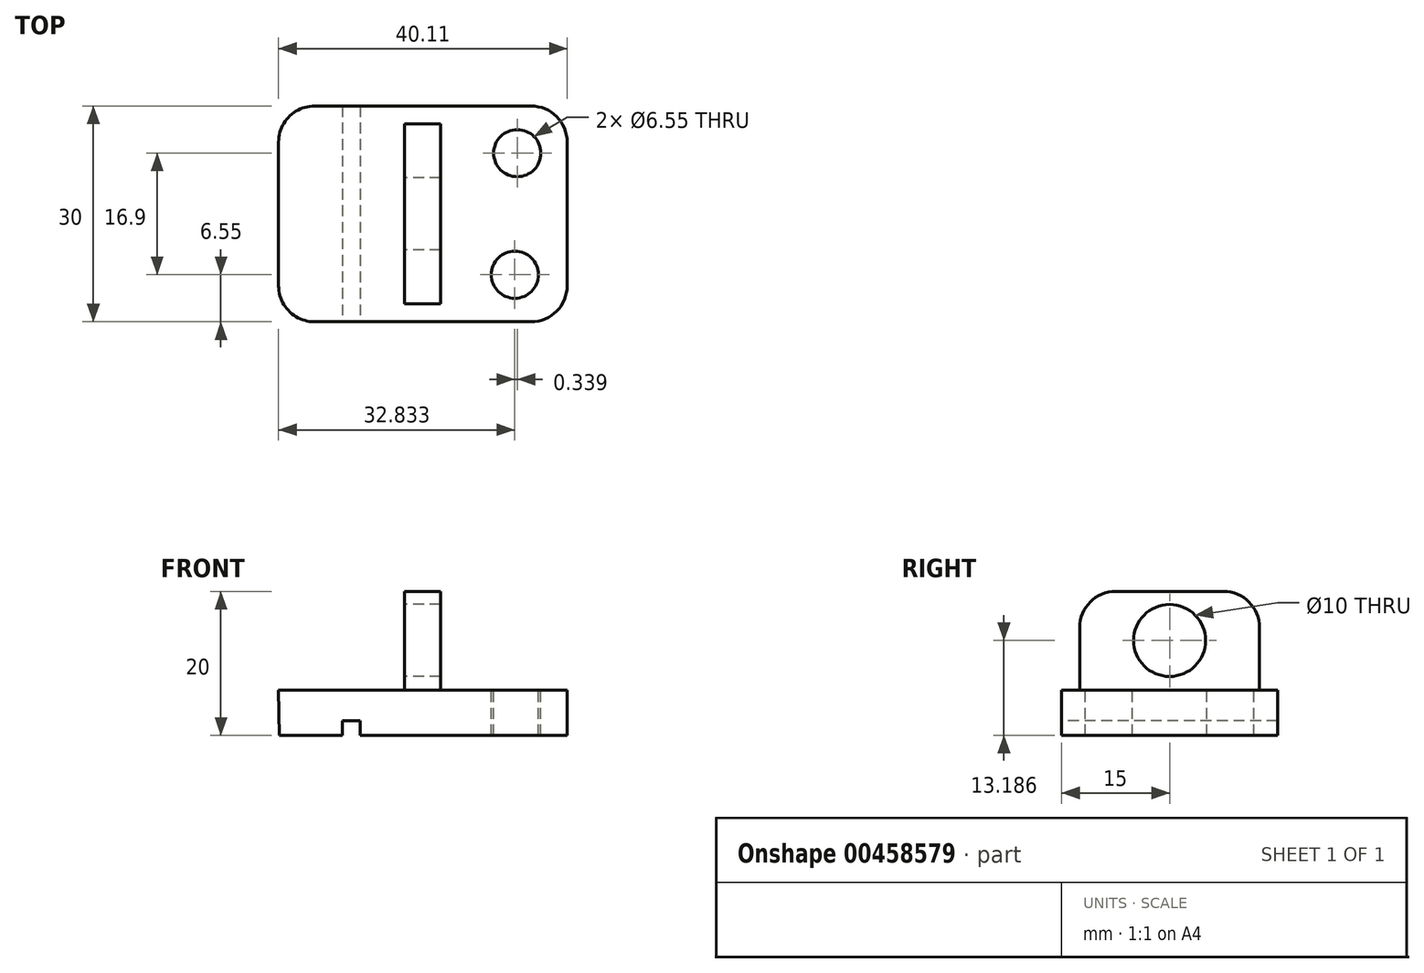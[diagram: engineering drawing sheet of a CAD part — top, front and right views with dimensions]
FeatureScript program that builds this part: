
annotation { "Feature Type Name" : "Feature", "Feature Type Description" : "" }
export const myFeature = defineFeature(function(context is Context, id is Id, definition is map)
    precondition{}
    {
        {
            var Q0;
            Q0=qCreatedBy(makeId("Front.planeOp"),FACE);
            var sketch = newSketch(context, id + "F0", { "sketchPlane" : qUnion([Q0])});
            skLineSegment(sketch, "E0", {"start": v(-11.08, -16.5) * mm, "end": v(29.03, -16.5) * mm});
            skLineSegment(sketch, "E1", {"start": v(29.03, -16.5) * mm, "end": v(29.03, -22.75) * mm});
            skLineSegment(sketch, "E2", {"start": v(29.03, -22.75) * mm, "end": v(-10.97, -22.75) * mm});
            skLineSegment(sketch, "E3", {"start": v(-10.97, -22.75) * mm, "end": v(-11.08, -16.5) * mm});
            skLineSegment(sketch, "E4", {"start": v(6.42, -16.5) * mm, "end": v(6.42, -2.75) * mm});
            skLineSegment(sketch, "E5", {"start": v(6.42, -2.75) * mm, "end": v(11.42, -2.75) * mm});
            skLineSegment(sketch, "E6", {"start": v(11.42, -2.75) * mm, "end": v(11.42, -16.5) * mm});
            skSolve(sketch);
        }
        {
            var Q0;
            {var subQ0=sQuery(id+"F0.wireOp",EDGE,"E1");Q0=makeQuery(id+"F0.imprint","IMPRINT",FACE,{"disambiguationData":[TD([[makeQuery(id+"F0.imprint","IMPRINT",EDGE,{"derivedFrom":subQ0}),-1.0]])]});}
            extrude(context, id + "F1", {"entities" : qUnion([Q0]), "endBound" : BoundingType.SYMMETRIC, "depth" : 30 * mm});
        }
        {
            var Q0;
            Q0 = qSketchRegion(id + "F0", true);
            extrude(context, id + "F2", {"entities" : qUnion([Q0]), "operationType" : NewBodyOperationType.ADD, "endBound" : BoundingType.SYMMETRIC, "depth" : 25 * mm});
        }
        {
            var Q0;
            Q0=qCreatedBy(makeId("Front.planeOp"),FACE);
            var sketch = newSketch(context, id + "F3", { "sketchPlane" : qUnion([Q0])});
            skLineSegment(sketch, "E7", {"start": v(-2.22, -22.75) * mm, "end": v(-2.22, -20.75) * mm});
            skLineSegment(sketch, "E8", {"start": v(-2.22, -20.75) * mm, "end": v(0.28, -20.75) * mm});
            skLineSegment(sketch, "E9", {"start": v(0.28, -20.75) * mm, "end": v(0.28, -22.75) * mm});
            skLineSegment(sketch, "E10", {"start": v(-2.22, -22.75) * mm, "end": v(0.28, -22.75) * mm});
            skSolve(sketch);
        }
        {
            var Q0;
            Q0=makeQuery(id+"F1.opExtrude","CAP_EDGE",EDGE,{"disambiguationData":[OSD([sQuery(id+"F0.wireOp",EDGE,"E1")])],"isStart":false});
            fillet(context, id + "F4", {"entities" : qUnion([Q0]), "radius" : 5 * mm, "tangentPropagation" : true, "allowEdgeOverflow" : false});
        }
        {
            var Q0;
            Q0=makeQuery(id+"F1.opExtrude","CAP_EDGE",EDGE,{"disambiguationData":[OSD([sQuery(id+"F0.wireOp",EDGE,"E1")])],"isStart":true});
            var Q1;
            Q1=makeQuery(id+"F1.opExtrude","CAP_EDGE",EDGE,{"disambiguationData":[OSD([sQuery(id+"F0.wireOp",EDGE,"E3")])],"isStart":false});
            var Q2;
            Q2=makeQuery(id+"F1.opExtrude","CAP_EDGE",EDGE,{"disambiguationData":[OSD([sQuery(id+"F0.wireOp",EDGE,"E3")])],"isStart":true});
            fillet(context, id + "F5", {"entities" : qUnion([Q0, Q1, Q2]), "radius" : 5 * mm, "tangentPropagation" : true, "allowEdgeOverflow" : false});
        }
        {
            var Q0;
            Q0=makeQuery(id+"F2.opExtrude","CAP_EDGE",EDGE,{"disambiguationData":[OSD([sQuery(id+"F0.wireOp",EDGE,"E5")])],"isStart":true});
            var Q1;
            Q1=makeQuery(id+"F2.opExtrude","CAP_EDGE",EDGE,{"disambiguationData":[OSD([sQuery(id+"F0.wireOp",EDGE,"E5")])],"isStart":false});
            fillet(context, id + "F6", {"entities" : qUnion([Q0, Q1]), "radius" : 5 * mm, "tangentPropagation" : true, "allowEdgeOverflow" : false});
        }
        {
            var Q0;
            Q0=qCreatedBy(makeId("Top.planeOp"),FACE);
            var sketch = newSketch(context, id + "F7", { "sketchPlane" : qUnion([Q0])});
            skCircle(sketch, "E11", {"center": v(21.75, -8.45) * mm, "radius": 3.28 * mm});
            skCircle(sketch, "E12", {"center": v(22.1, 8.45) * mm, "radius": 3.28 * mm});
            skSolve(sketch);
        }
        {
            var Q0;
            Q0=makeQuery(id+"F7.imprint","IMPRINT",FACE,{"disambiguationData":[TD([[makeQuery(id+"F7.imprint","IMPRINT",EDGE,{"derivedFrom":sQuery(id+"F7.wireOp",EDGE,"E12")}),1.0]])]});
            var Q1;
            Q1=makeQuery(id+"F7.imprint","IMPRINT",FACE,{"disambiguationData":[TD([[makeQuery(id+"F7.imprint","IMPRINT",EDGE,{"derivedFrom":sQuery(id+"F7.wireOp",EDGE,"E11")}),1.0]])]});
            extrude(context, id + "F8", {"entities" : qUnion([Q0, Q1]), "operationType" : NewBodyOperationType.REMOVE, "oppositeDirection" : true, "depth" : 25 * mm});
        }
        {
            var Q0;
            Q0 = qSketchRegion(id + "F3", true);
            extrude(context, id + "F9", {"entities" : qUnion([Q0]), "operationType" : NewBodyOperationType.REMOVE, "endBound" : BoundingType.SYMMETRIC, "oppositeDirection" : true, "depth" : 100 * mm});
        }
        {
            var Q0;
            Q0=qCreatedBy(makeId("Right.planeOp"),FACE);
            var sketch = newSketch(context, id + "F10", { "sketchPlane" : qUnion([Q0])});
            skCircle(sketch, "E13", {"center": v(0, -9.56) * mm, "radius": 5 * mm});
            skSolve(sketch);
        }
        {
            var Q0;
            Q0 = qSketchRegion(id + "F10", true);
            var Q1;
            Q1=sQuery(id+"F10.wireOp",EDGE,"E13");
            extrude(context, id + "F11", {"entities" : qUnion([Q0]), "operationType" : NewBodyOperationType.REMOVE, "surfaceEntities" : qUnion([Q1]), "endBound" : BoundingType.SYMMETRIC, "depth" : 60 * mm});
        }
    });
